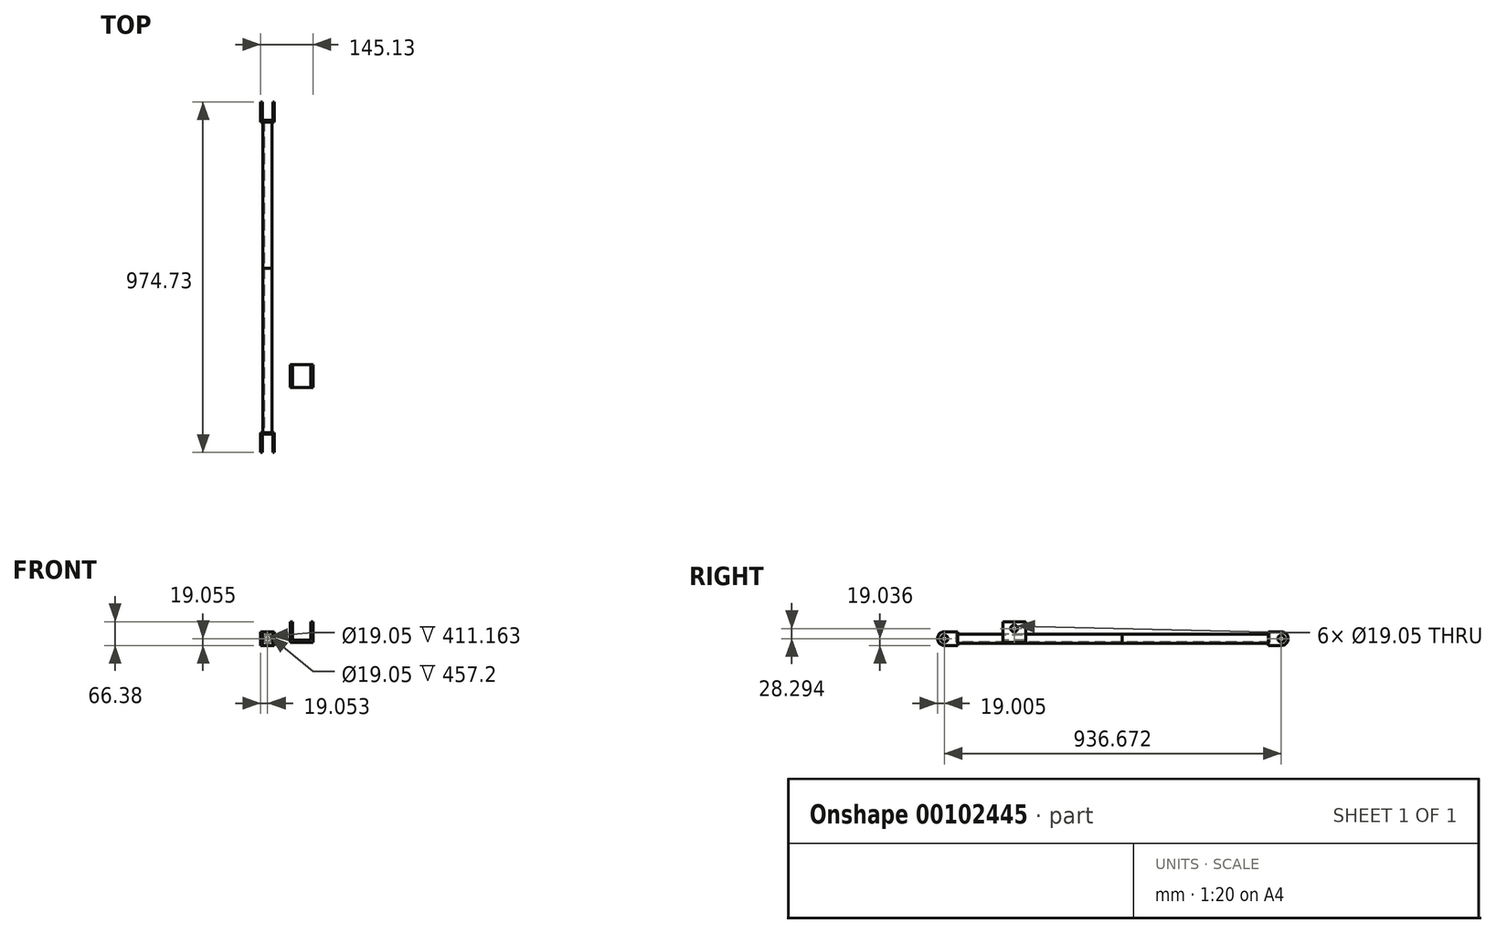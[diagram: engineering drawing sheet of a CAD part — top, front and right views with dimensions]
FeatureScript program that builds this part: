
annotation { "Feature Type Name" : "Feature", "Feature Type Description" : "" }
export const myFeature = defineFeature(function(context is Context, id is Id, definition is map)
    precondition{}
    {
        {
            var Q0;
            Q0=qCreatedBy(makeId("Right.planeOp"),FACE);
            var sketch = newSketch(context, id + "F0", { "sketchPlane" : qUnion([Q0])});
            skLineSegment(sketch, "E0.bottom", {"start": v(-173.45, 28.87) * mm, "end": v(-122.65, 28.87) * mm});
            skLineSegment(sketch, "E0.top", {"start": v(-173.45, -9.23) * mm, "end": v(-122.65, -9.23) * mm});
            skLineSegment(sketch, "E0.left", {"start": v(-173.45, 28.87) * mm, "end": v(-173.45, -9.23) * mm});
            skLineSegment(sketch, "E0.right", {"start": v(-122.65, 28.87) * mm, "end": v(-122.65, -9.23) * mm});
            skCircle(sketch, "E1", {"center": v(-154.4, 9.82) * mm, "radius": 9.53 * mm});
            skPoint(sketch, "E1.centerSnap0", {"position": v(-148.05, -9.23) * mm});
            skSolve(sketch);
        }
        {
            var Q0;
            Q0=makeQuery(id+"F0.imprint","IMPRINT",FACE,{"disambiguationData":[TD([[makeQuery(id+"F0.imprint","IMPRINT",EDGE,{"derivedFrom":sQuery(id+"F0.wireOp",EDGE,"E0.bottom")}),-1.0]])]});
            extrude(context, id + "F1", {"entities" : qUnion([Q0]), "depth" : 4.76 * mm});
        }
        {
            var Q0;
            Q0=makeQuery(id+"F1.opExtrude","SWEPT_EDGE",EDGE,{"disambiguationData":[OSD([sQuery(id+"F0.wireOp",EDGE,"E0.bottom"),sQuery(id+"F0.wireOp",EDGE,"E0.left")])]});
            var Q1;
            Q1=makeQuery(id+"F1.opExtrude","SWEPT_EDGE",EDGE,{"disambiguationData":[OSD([sQuery(id+"F0.wireOp",EDGE,"E0.top"),sQuery(id+"F0.wireOp",EDGE,"E0.left")])]});
            fillet(context, id + "F2", {"entities" : qUnion([Q0, Q1]), "radius" : 19.05 * mm, "tangentPropagation" : true, "allowEdgeOverflow" : false});
        }
        {
            var Q0;
            Q0=makeQuery(id+"F1.opExtrude","SWEPT_FACE",FACE,{"disambiguationData":[OSD([sQuery(id+"F0.wireOp",EDGE,"E0.right")])]});
            var sketch = newSketch(context, id + "F3", { "sketchPlane" : qUnion([Q0])});
            skLineSegment(sketch, "E2.bottom", {"start": v(-4.76, 28.87) * mm, "end": v(33.34, 28.87) * mm});
            skLineSegment(sketch, "E2.top", {"start": v(-4.76, -9.23) * mm, "end": v(33.34, -9.23) * mm});
            skLineSegment(sketch, "E2.left", {"start": v(-4.76, 28.87) * mm, "end": v(-4.76, -9.23) * mm});
            skLineSegment(sketch, "E2.right", {"start": v(33.34, 28.87) * mm, "end": v(33.34, -9.23) * mm});
            skSolve(sketch);
        }
        {
            var Q0;
            {var subQ2=sQuery(id+"F3.wireOp",EDGE,"E2.right");Q0=makeQuery(id+"F3.imprint","IMPRINT",FACE,{"disambiguationData":[TD([[makeQuery(id+"F3.imprint","IMPRINT",EDGE,{"derivedFrom":subQ2}),-1.0]])]});}
            var Q1;
            {var subQ2=sQuery(id+"F3.wireOp",EDGE,"E2.left");Q1=makeQuery(id+"F3.imprint","IMPRINT",FACE,{"disambiguationData":[TD([[makeQuery(id+"F3.imprint","IMPRINT",EDGE,{"derivedFrom":subQ2}),1.0]])]});}
            extrude(context, id + "F4", {"entities" : qUnion([Q0, Q1]), "operationType" : NewBodyOperationType.ADD, "depth" : 4.76 * mm});
        }
        {
            var Q0;
            Q0=makeQuery(id+"F4.opExtrude","SWEPT_FACE",FACE,{"disambiguationData":[OSD([sQuery(id+"F3.wireOp",EDGE,"E2.right")])]});
            var sketch = newSketch(context, id + "F5", { "sketchPlane" : qUnion([Q0])});
            skLineSegment(sketch, "E3.bottom", {"start": v(122.65, 28.87) * mm, "end": v(173.45, 28.87) * mm});
            skLineSegment(sketch, "E3.top", {"start": v(122.65, -9.23) * mm, "end": v(173.45, -9.23) * mm});
            skLineSegment(sketch, "E3.left", {"start": v(122.65, 28.87) * mm, "end": v(122.65, -9.23) * mm});
            skLineSegment(sketch, "E3.right", {"start": v(173.45, 28.87) * mm, "end": v(173.45, -9.23) * mm});
            skCircle(sketch, "E4", {"center": v(154.44, 9.8) * mm, "radius": 9.53 * mm});
            skSolve(sketch);
        }
        {
            var Q0;
            Q0=makeQuery(id+"F5.imprint","IMPRINT",FACE,{"disambiguationData":[TD([[makeQuery(id+"F5.imprint","IMPRINT",EDGE,{"derivedFrom":sQuery(id+"F5.wireOp",EDGE,"E3.bottom")}),-1.0]])]});
            extrude(context, id + "F6", {"entities" : qUnion([Q0]), "operationType" : NewBodyOperationType.ADD, "oppositeDirection" : true, "depth" : 4.76 * mm});
        }
        {
            var Q0;
            Q0=makeQuery(id+"F6.opExtrude","SWEPT_EDGE",EDGE,{"disambiguationData":[OSD([sQuery(id+"F5.wireOp",EDGE,"E3.bottom"),sQuery(id+"F5.wireOp",EDGE,"E3.right")])]});
            var Q1;
            Q1=makeQuery(id+"F6.opExtrude","SWEPT_EDGE",EDGE,{"disambiguationData":[OSD([sQuery(id+"F5.wireOp",EDGE,"E3.top"),sQuery(id+"F5.wireOp",EDGE,"E3.right")])]});
            fillet(context, id + "F7", {"entities" : qUnion([Q0, Q1]), "radius" : 19.05 * mm, "tangentPropagation" : true, "allowEdgeOverflow" : false});
        }
        {
            var Q0;
            Q0=makeQuery(id+"F4.opExtrude","CAP_FACE",FACE,{"disambiguationData":[OSD([sQuery(id+"F3.wireOp",EDGE,"E2.bottom"),sQuery(id+"F3.wireOp",EDGE,"E2.top"),sQuery(id+"F3.wireOp",EDGE,"E2.left"),sQuery(id+"F3.wireOp",EDGE,"E2.right")])],"isStart":false});
            var sketch = newSketch(context, id + "F8", { "sketchPlane" : qUnion([Q0])});
            skCircle(sketch, "E5", {"center": v(14.29, 9.82) * mm, "radius": 12.7 * mm});
            skPoint(sketch, "E6", {"position": v(33.34, 9.82) * mm});
            skPoint(sketch, "E7", {"position": v(14.29, -9.23) * mm});
            skSolve(sketch);
        }
        {
            var Q0;
            Q0=makeQuery(id+"F8.imprint","IMPRINT",FACE,{"disambiguationData":[TD([[makeQuery(id+"F8.imprint","IMPRINT",EDGE,{"derivedFrom":sQuery(id+"F8.wireOp",EDGE,"E5")}),1.0]])]});
            extrude(context, id + "F9", {"entities" : qUnion([Q0]), "operationType" : NewBodyOperationType.ADD, "depth" : 457.2 * mm});
        }
        {
            var Q0;
            Q0=makeQuery(id+"F9.opExtrude","CAP_FACE",FACE,{"disambiguationData":[OSD([sQuery(id+"F8.wireOp",EDGE,"E5")])],"isStart":false});
            var sketch = newSketch(context, id + "F10", { "sketchPlane" : qUnion([Q0])});
            skPoint(sketch, "E8", {"position": v(14.29, 9.82) * mm});
            skSolve(sketch);
        }
        {
            var Q0;
            Q0=sQuery(id+"F10.wireOp",VERTEX,"E8");
            var Q1;
            Q1=makeQuery(id+"F1.opExtrude","SWEPT_BODY",BODY,{"disambiguationData":[OSD([sQuery(id+"F0.wireOp",EDGE,"E0.bottom"),sQuery(id+"F0.wireOp",EDGE,"E0.top"),sQuery(id+"F0.wireOp",EDGE,"E0.left"),sQuery(id+"F0.wireOp",EDGE,"E0.right"),sQuery(id+"F0.wireOp",EDGE,"E1")])]});
            hole(context, id + "F11", {"style" : HoleStyle.SIMPLE, "endStyle" : HoleEndStyle.BLIND, "holeDiameter" : 19.05 * mm, "holeDepth" : 457.2 * mm, "locations" : qUnion([Q0]), "scope" : qUnion([Q1]), "startStyle" : HoleStartStyle.SKETCH});
        }
        {
            var Q0;
            Q0=makeQuery(id+"F9.opExtrude","CAP_FACE",FACE,{"disambiguationData":[OSD([sQuery(id+"F8.wireOp",EDGE,"E5")])],"isStart":false});
            var sketch = newSketch(context, id + "F12", { "sketchPlane" : qUnion([Q0])});
            skCircle(sketch, "E9", {"center": v(14.29, 9.82) * mm, "radius": 9.53 * mm});
            skSolve(sketch);
        }
        {
            var Q0;
            Q0=makeQuery(id+"F12.imprint","IMPRINT",FACE,{"disambiguationData":[TD([[makeQuery(id+"F12.imprint","IMPRINT",EDGE,{"derivedFrom":sQuery(id+"F12.wireOp",EDGE,"E9")}),1.0]])]});
            extrude(context, id + "F13", {"entities" : qUnion([Q0]), "depth" : 406.4 * mm});
        }
        {
            var Q0;
            Q0=makeQuery(id+"F13.opExtrude","CAP_FACE",FACE,{"disambiguationData":[OSD([sQuery(id+"F12.wireOp",EDGE,"E9")])],"isStart":false});
            var sketch = newSketch(context, id + "F14", { "sketchPlane" : qUnion([Q0])});
            skLineSegment(sketch, "E10.bottom", {"start": v(-4.76, 28.88) * mm, "end": v(33.34, 28.88) * mm});
            skLineSegment(sketch, "E10.top", {"start": v(-4.76, -9.22) * mm, "end": v(33.34, -9.22) * mm});
            skLineSegment(sketch, "E10.left", {"start": v(-4.76, 28.88) * mm, "end": v(-4.76, -9.22) * mm});
            skLineSegment(sketch, "E10.right", {"start": v(33.34, 28.88) * mm, "end": v(33.34, -9.22) * mm});
            skSolve(sketch);
        }
        {
            var Q0;
            Q0=makeQuery(id+"F14.imprint","IMPRINT",FACE,{"disambiguationData":[TD([[makeQuery(id+"F14.imprint","IMPRINT",EDGE,{"derivedFrom":sQuery(id+"F14.wireOp",EDGE,"E10.bottom")}),-1.0]])]});
            var Q1;
            Q1=makeQuery(id+"F14.imprint","IMPRINT",FACE,{"disambiguationData":[TD([[makeQuery(id+"F14.imprint","IMPRINT",EDGE,{"derivedFrom":makeQuery(id+"F13.opExtrude","CAP_EDGE",EDGE,{"disambiguationData":[OSD([sQuery(id+"F12.wireOp",EDGE,"E9")])],"isStart":false})}),1.0]])]});
            extrude(context, id + "F15", {"entities" : qUnion([Q0, Q1]), "operationType" : NewBodyOperationType.ADD, "depth" : 4.76 * mm});
        }
        {
            var Q0;
            Q0=makeQuery(id+"F15.opExtrude","SWEPT_FACE",FACE,{"disambiguationData":[OSD([sQuery(id+"F14.wireOp",EDGE,"E10.left")])]});
            var sketch = newSketch(context, id + "F16", { "sketchPlane" : qUnion([Q0])});
            skLineSegment(sketch, "E11.bottom", {"start": v(750.48, 28.88) * mm, "end": v(801.28, 28.88) * mm});
            skLineSegment(sketch, "E11.top", {"start": v(750.48, -9.22) * mm, "end": v(801.28, -9.22) * mm});
            skLineSegment(sketch, "E11.left", {"start": v(750.48, 28.88) * mm, "end": v(750.48, -9.22) * mm});
            skLineSegment(sketch, "E11.right", {"start": v(801.28, 28.88) * mm, "end": v(801.28, -9.22) * mm});
            skCircle(sketch, "E12", {"center": v(782.23, 9.83) * mm, "radius": 9.53 * mm});
            skPoint(sketch, "E12.centerSnap0", {"position": v(801.28, 9.83) * mm});
            skPoint(sketch, "E12.centerSnap1", {"position": v(775.88, -9.22) * mm});
            skSolve(sketch);
        }
        {
            var Q0;
            Q0=makeQuery(id+"F16.imprint","IMPRINT",FACE,{"disambiguationData":[TD([[makeQuery(id+"F16.imprint","IMPRINT",EDGE,{"derivedFrom":sQuery(id+"F16.wireOp",EDGE,"E11.bottom")}),-1.0]])]});
            extrude(context, id + "F17", {"entities" : qUnion([Q0]), "operationType" : NewBodyOperationType.ADD, "oppositeDirection" : true, "depth" : 4.76 * mm});
        }
        {
            var Q0;
            Q0=makeQuery(id+"F17.opExtrude","SWEPT_EDGE",EDGE,{"disambiguationData":[OSD([sQuery(id+"F16.wireOp",EDGE,"E11.bottom"),sQuery(id+"F16.wireOp",EDGE,"E11.right")])]});
            var Q1;
            Q1=makeQuery(id+"F17.opExtrude","SWEPT_EDGE",EDGE,{"disambiguationData":[OSD([sQuery(id+"F16.wireOp",EDGE,"E11.top"),sQuery(id+"F16.wireOp",EDGE,"E11.right")])]});
            fillet(context, id + "F18", {"entities" : qUnion([Q0, Q1]), "radius" : 19.05 * mm, "tangentPropagation" : true, "allowEdgeOverflow" : false});
        }
        {
            var Q0;
            Q0=makeQuery(id+"F15.opExtrude","SWEPT_FACE",FACE,{"disambiguationData":[OSD([sQuery(id+"F14.wireOp",EDGE,"E10.right")])]});
            var sketch = newSketch(context, id + "F19", { "sketchPlane" : qUnion([Q0])});
            skLineSegment(sketch, "E13.bottom", {"start": v(-750.48, 28.88) * mm, "end": v(-801.28, 28.88) * mm});
            skLineSegment(sketch, "E13.top", {"start": v(-750.48, -9.22) * mm, "end": v(-801.28, -9.22) * mm});
            skLineSegment(sketch, "E13.left", {"start": v(-750.48, 28.88) * mm, "end": v(-750.48, -9.22) * mm});
            skLineSegment(sketch, "E13.right", {"start": v(-801.28, 28.88) * mm, "end": v(-801.28, -9.22) * mm});
            skCircle(sketch, "E14", {"center": v(-782.23, 9.83) * mm, "radius": 9.53 * mm});
            skSolve(sketch);
        }
        {
            var Q0;
            Q0=makeQuery(id+"F19.imprint","IMPRINT",FACE,{"disambiguationData":[TD([[makeQuery(id+"F19.imprint","IMPRINT",EDGE,{"derivedFrom":sQuery(id+"F19.wireOp",EDGE,"E13.bottom")}),1.0]])]});
            extrude(context, id + "F20", {"entities" : qUnion([Q0]), "operationType" : NewBodyOperationType.ADD, "oppositeDirection" : true, "depth" : 4.76 * mm});
        }
        {
            var Q0;
            Q0=makeQuery(id+"F20.opExtrude","SWEPT_EDGE",EDGE,{"disambiguationData":[OSD([sQuery(id+"F19.wireOp",EDGE,"E13.bottom"),sQuery(id+"F19.wireOp",EDGE,"E13.right")])]});
            var Q1;
            Q1=makeQuery(id+"F20.opExtrude","SWEPT_EDGE",EDGE,{"disambiguationData":[OSD([sQuery(id+"F19.wireOp",EDGE,"E13.top"),sQuery(id+"F19.wireOp",EDGE,"E13.right")])]});
            fillet(context, id + "F21", {"entities" : qUnion([Q0, Q1]), "radius" : 19.05 * mm, "tangentPropagation" : true, "allowEdgeOverflow" : false});
        }
        {
            var Q0;
            Q0=qCreatedBy(makeId("Top.planeOp"),FACE);
            var sketch = newSketch(context, id + "F22", { "sketchPlane" : qUnion([Q0])});
            skLineSegment(sketch, "E15.bottom", {"start": v(48.3, 71.28) * mm, "end": v(111.8, 71.28) * mm});
            skLineSegment(sketch, "E15.top", {"start": v(48.3, 7.78) * mm, "end": v(111.8, 7.78) * mm});
            skLineSegment(sketch, "E15.left", {"start": v(48.3, 71.28) * mm, "end": v(48.3, 7.78) * mm});
            skLineSegment(sketch, "E15.right", {"start": v(111.8, 71.28) * mm, "end": v(111.8, 7.78) * mm});
            skSolve(sketch);
        }
        {
            var Q0;
            Q0=makeQuery(id+"F22.imprint","IMPRINT",FACE,{"disambiguationData":[TD([[makeQuery(id+"F22.imprint","IMPRINT",EDGE,{"derivedFrom":sQuery(id+"F22.wireOp",EDGE,"E15.bottom")}),-1.0]])]});
            extrude(context, id + "F23", {"entities" : qUnion([Q0]), "depth" : 6.35 * mm});
        }
        {
            var Q0;
            Q0=makeQuery(id+"F23.opExtrude","SWEPT_FACE",FACE,{"disambiguationData":[OSD([sQuery(id+"F22.wireOp",EDGE,"E15.right")])]});
            var sketch = newSketch(context, id + "F24", { "sketchPlane" : qUnion([Q0])});
            skLineSegment(sketch, "E16.bottom", {"start": v(71.28, 6.35) * mm, "end": v(7.78, 6.35) * mm});
            skLineSegment(sketch, "E16.top", {"start": v(71.28, 57.15) * mm, "end": v(7.78, 57.15) * mm});
            skLineSegment(sketch, "E16.left", {"start": v(71.28, 6.35) * mm, "end": v(71.28, 57.15) * mm});
            skLineSegment(sketch, "E16.right", {"start": v(7.78, 6.35) * mm, "end": v(7.78, 57.15) * mm});
            skCircle(sketch, "E17", {"center": v(39.53, 38.1) * mm, "radius": 9.53 * mm});
            skPoint(sketch, "E17.centerSnap0", {"position": v(39.53, 57.15) * mm});
            skSolve(sketch);
        }
        {
            var Q0;
            Q0=makeQuery(id+"F24.imprint","IMPRINT",FACE,{"disambiguationData":[TD([[makeQuery(id+"F24.imprint","IMPRINT",EDGE,{"derivedFrom":sQuery(id+"F24.wireOp",EDGE,"E16.bottom")}),-1.0]])]});
            extrude(context, id + "F25", {"entities" : qUnion([Q0]), "operationType" : NewBodyOperationType.ADD, "oppositeDirection" : true, "depth" : 6.35 * mm});
        }
        {
            var Q0;
            Q0=makeQuery(id+"F23.opExtrude","SWEPT_FACE",FACE,{"disambiguationData":[OSD([sQuery(id+"F22.wireOp",EDGE,"E15.left")])]});
            var sketch = newSketch(context, id + "F26", { "sketchPlane" : qUnion([Q0])});
            skLineSegment(sketch, "E18.bottom", {"start": v(-7.78, 6.35) * mm, "end": v(-71.28, 6.35) * mm});
            skLineSegment(sketch, "E18.top", {"start": v(-7.78, 57.15) * mm, "end": v(-71.28, 57.15) * mm});
            skLineSegment(sketch, "E18.left", {"start": v(-7.78, 6.35) * mm, "end": v(-7.78, 57.15) * mm});
            skLineSegment(sketch, "E18.right", {"start": v(-71.28, 6.35) * mm, "end": v(-71.28, 57.15) * mm});
            skCircle(sketch, "E19", {"center": v(-39.53, 38.1) * mm, "radius": 9.53 * mm});
            skSolve(sketch);
        }
        {
            var Q0;
            Q0=makeQuery(id+"F26.imprint","IMPRINT",FACE,{"disambiguationData":[TD([[makeQuery(id+"F26.imprint","IMPRINT",EDGE,{"derivedFrom":sQuery(id+"F26.wireOp",EDGE,"E18.bottom")}),1.0]])]});
            extrude(context, id + "F27", {"entities" : qUnion([Q0]), "operationType" : NewBodyOperationType.ADD, "oppositeDirection" : true, "depth" : 6.35 * mm});
        }
    });
